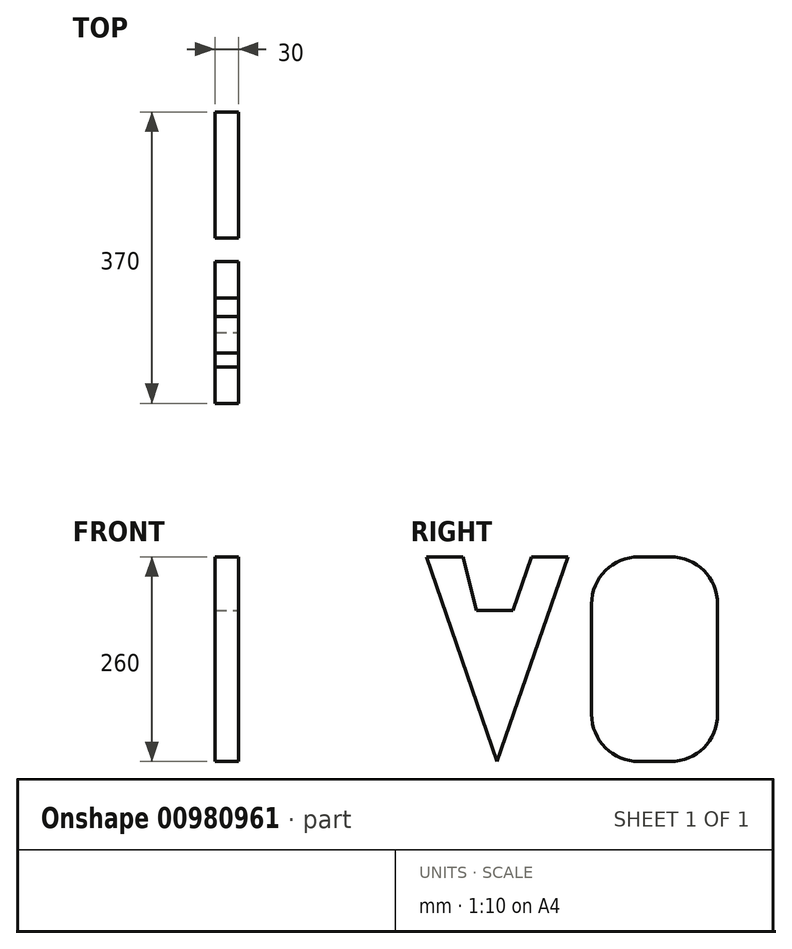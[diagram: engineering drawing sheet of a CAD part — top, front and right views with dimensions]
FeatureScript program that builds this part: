
annotation { "Feature Type Name" : "Feature", "Feature Type Description" : "" }
export const myFeature = defineFeature(function(context is Context, id is Id, definition is map)
    precondition{}
    {
        {
            var Q0;
            Q0=qCreatedBy(makeId("Right.planeOp"),FACE);
            cPlane(context, id + "F0", {"entities" : qUnion([Q0]), "cplaneType" : CPlaneType.OFFSET, "offset" : 30 * mm, "width" : 150 * mm, "height" : 150 * mm});
        }
        {
            var Q0;
            Q0=qCreatedBy(id+"F0.planeOp",FACE);
            var sketch = newSketch(context, id + "F1", { "sketchPlane" : qUnion([Q0])});
            skLineSegment(sketch, "E0", {"start": v(-190, 120) * mm, "end": v(-100, -140) * mm});
            skLineSegment(sketch, "E1", {"start": v(-100, -140) * mm, "end": v(-10, 120) * mm});
            skLineSegment(sketch, "E2", {"start": v(-10, 120) * mm, "end": v(-56.31, 120) * mm});
            skLineSegment(sketch, "E3", {"start": v(-56.31, 120) * mm, "end": v(-79.86, 51.98) * mm});
            skLineSegment(sketch, "E4", {"start": v(-79.86, 51.98) * mm, "end": v(-126.17, 51.98) * mm});
            skLineSegment(sketch, "E5", {"start": v(-126.17, 51.98) * mm, "end": v(-143.69, 120) * mm});
            skLineSegment(sketch, "E6", {"start": v(-143.69, 120) * mm, "end": v(-190, 120) * mm});
            skLineSegment(sketch, "E7.bottom", {"start": v(80, 120) * mm, "end": v(120, 120) * mm});
            skLineSegment(sketch, "E7.top", {"start": v(80, -140) * mm, "end": v(120, -140) * mm});
            skLineSegment(sketch, "E7.left", {"start": v(20, 60) * mm, "end": v(20, -80) * mm});
            skLineSegment(sketch, "E7.right", {"start": v(180, 60) * mm, "end": v(180, -80) * mm});
            skPoint(sketch, "E8.visualSharp", {"position": v(20, 120) * mm});
            skArc(sketch, "E8.filletArc", {"start": v(80, 120) * mm, "mid": v(37.57, 102.43) * mm, "end": v(20, 60) * mm});
            skPoint(sketch, "E9.visualSharp", {"position": v(180, 120) * mm});
            skArc(sketch, "E9.filletArc", {"start": v(180, 60) * mm, "mid": v(162.43, 102.43) * mm, "end": v(120, 120) * mm});
            skPoint(sketch, "E10.visualSharp", {"position": v(20, -140) * mm});
            skArc(sketch, "E10.filletArc", {"start": v(20, -80) * mm, "mid": v(37.57, -122.43) * mm, "end": v(80, -140) * mm});
            skPoint(sketch, "E11.visualSharp", {"position": v(180, -140) * mm});
            skArc(sketch, "E11.filletArc", {"start": v(120, -140) * mm, "mid": v(162.43, -122.43) * mm, "end": v(180, -80) * mm});
            skSolve(sketch);
        }
        {
            var Q0;
            Q0=makeQuery(id+"F1.imprint","IMPRINT",FACE,{"disambiguationData":[TD([[makeQuery(id+"F1.imprint","IMPRINT",EDGE,{"derivedFrom":sQuery(id+"F1.wireOp",EDGE,"E0")}),1.0]])]});
            var Q1;
            Q1=makeQuery(id+"F1.imprint","IMPRINT",FACE,{"disambiguationData":[TD([[makeQuery(id+"F1.imprint","IMPRINT",EDGE,{"derivedFrom":sQuery(id+"F1.wireOp",EDGE,"E7.bottom")}),-1.0]])]});
            extrude(context, id + "F2", {"entities" : qUnion([Q0, Q1]), "oppositeDirection" : true, "depth" : 30 * mm, "offsetDistance" : 25 * mm});
        }
    });
